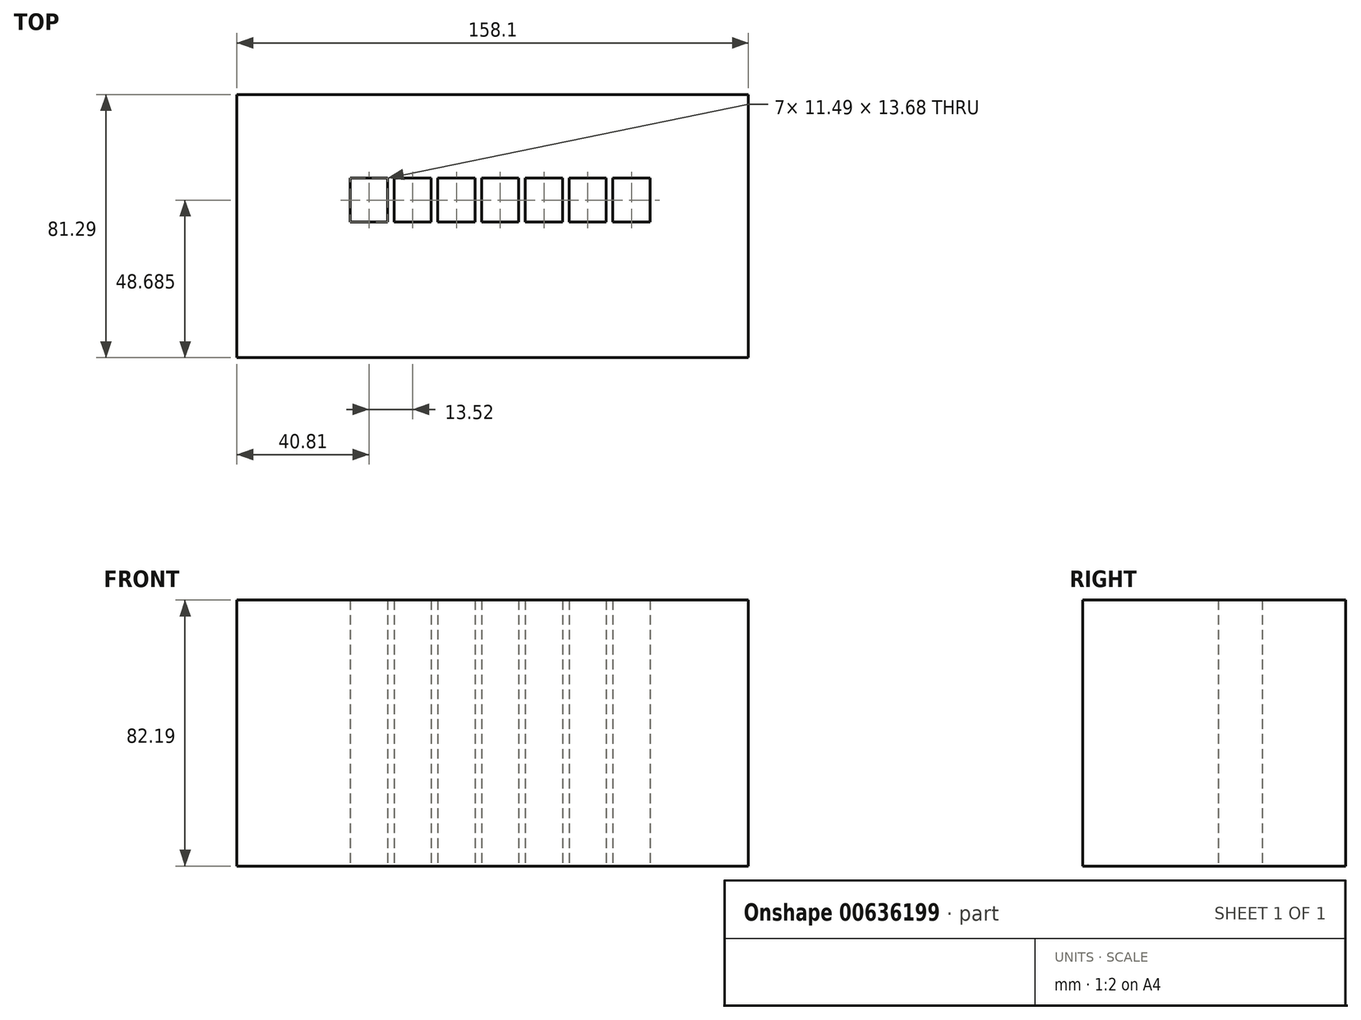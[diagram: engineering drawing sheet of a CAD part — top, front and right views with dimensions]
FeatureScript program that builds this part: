
annotation { "Feature Type Name" : "Feature", "Feature Type Description" : "" }
export const myFeature = defineFeature(function(context is Context, id is Id, definition is map)
    precondition{}
    {
        {
            var Q0;
            Q0=qCreatedBy(makeId("Top.planeOp"),FACE);
            var sketch = newSketch(context, id + "F0", { "sketchPlane" : qUnion([Q0])});
            skLineSegment(sketch, "E0.bottom", {"start": v(66.65, 21.04) * mm, "end": v(-91.45, 21.04) * mm});
            skLineSegment(sketch, "E0.top", {"start": v(66.65, 102.33) * mm, "end": v(-91.45, 102.33) * mm});
            skLineSegment(sketch, "E0.left", {"start": v(66.65, 21.04) * mm, "end": v(66.65, 102.33) * mm});
            skLineSegment(sketch, "E0.right", {"start": v(-91.45, 21.04) * mm, "end": v(-91.45, 102.33) * mm});
            skText(sketch, "E1", { "text": "高顏值瘋狂無腦", "fontName": "OpenSans-Regular.ttf"});
            skPoint(sketch, "E1.secondSnap0", {"position": v(66.65, 61.68) * mm});
            const initialGuessF0  = {"E1": [-0.0574, 0.06168, 1, 0, 0.01609]};
            skSetInitialGuess(sketch, initialGuessF0);
            skSolve(sketch);
        }
        {
            var Q0;
            Q0=makeQuery(id+"F0.imprint","IMPRINT",FACE,{"disambiguationData":[TD([[makeQuery(id+"F0.imprint","IMPRINT",EDGE,{"derivedFrom":sQuery(id+"F0.wireOp",EDGE,"E0.bottom")}),-1.0]])]});
            extrude(context, id + "F1", {"entities" : qUnion([Q0]), "depth" : 82.2 * mm, "offsetDistance" : 25 * mm});
        }
    });
